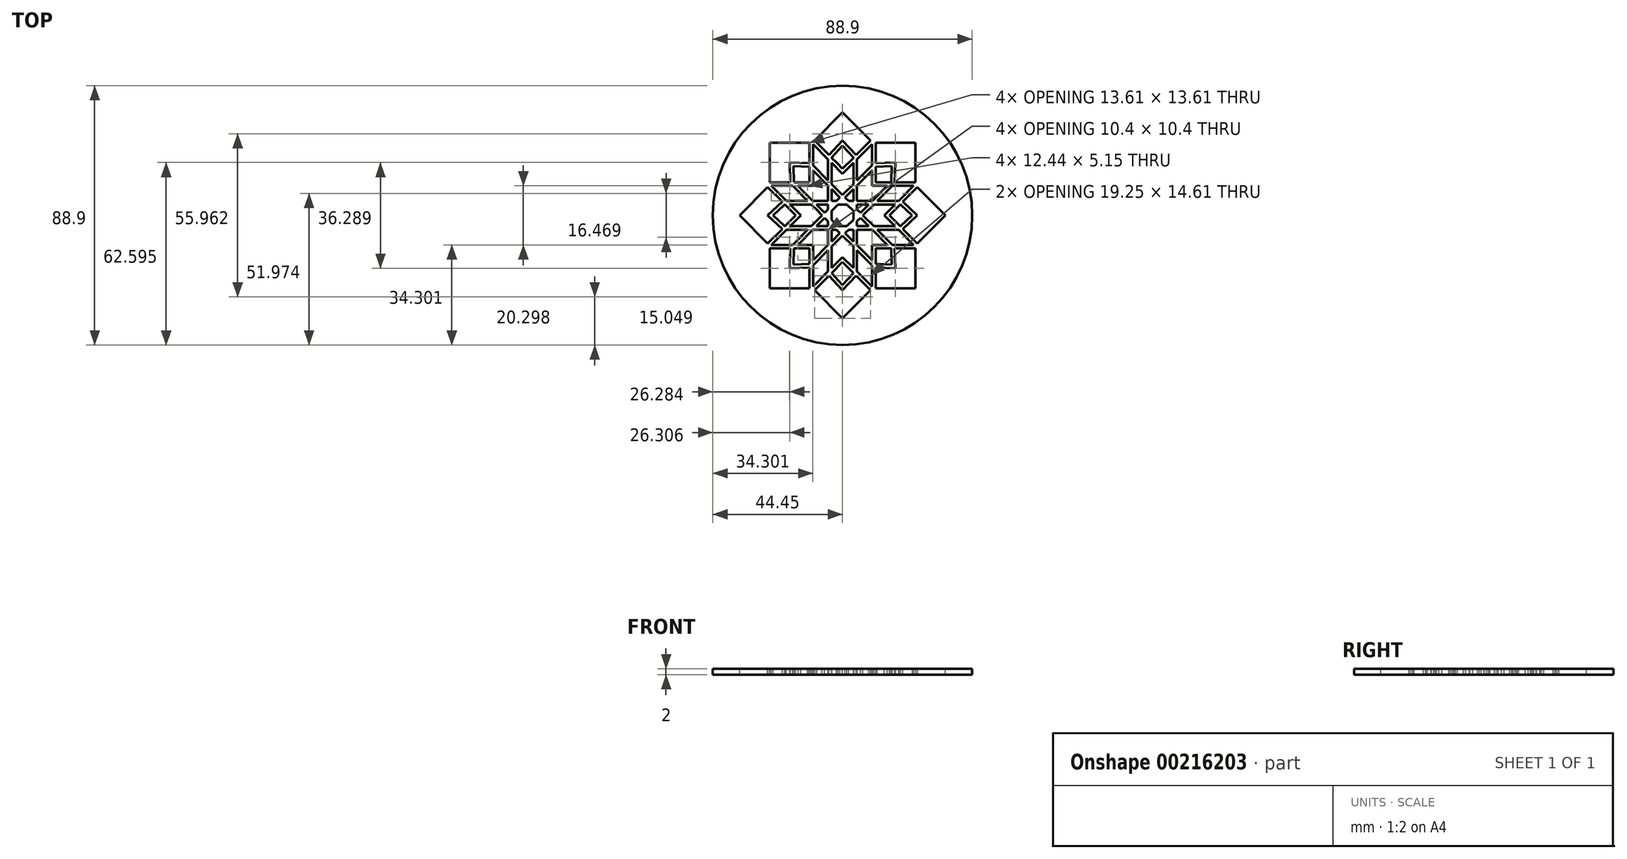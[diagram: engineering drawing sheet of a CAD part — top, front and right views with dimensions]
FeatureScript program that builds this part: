
annotation { "Feature Type Name" : "Feature", "Feature Type Description" : "" }
export const myFeature = defineFeature(function(context is Context, id is Id, definition is map)
    precondition{}
    {
        {
            var Q0;
            Q0=qCreatedBy(makeId("Top.planeOp"),FACE);
            var sketch = newSketch(context, id + "F0", { "sketchPlane" : qUnion([Q0])});
            skLineSegment(sketch, "E0.bottom", {"start": v(-44.45, 44.45) * mm, "end": v(44.45, 44.45) * mm});
            skLineSegment(sketch, "E0.top", {"start": v(-44.45, -44.45) * mm, "end": v(44.45, -44.45) * mm});
            skLineSegment(sketch, "E0.left", {"start": v(-44.45, 44.45) * mm, "end": v(-44.45, -44.45) * mm});
            skLineSegment(sketch, "E0.right", {"start": v(44.45, 44.45) * mm, "end": v(44.45, -44.45) * mm});
            skSolve(sketch);
        }
        {
            var Q0;
            Q0 = qSketchRegion(id + "F0", true);
            extrude(context, id + "F1", {"entities" : qUnion([Q0]), "oppositeDirection" : true, "depth" : 2 * mm});
        }
        {
            var Q0;
            Q0=qCreatedBy(makeId("Top.planeOp"),FACE);
            var sketch = newSketch(context, id + "F2", { "sketchPlane" : qUnion([Q0])});
            skLineSegment(sketch, "E1", {"start": v(0.87, 6.12) * mm, "end": v(2.05, 4.95) * mm});
            skLineSegment(sketch, "E2", {"start": v(2.05, 4.95) * mm, "end": v(3.71, 4.95) * mm});
            skLineSegment(sketch, "E3", {"start": v(3.71, 4.95) * mm, "end": v(3.71, 8.96) * mm});
            skLineSegment(sketch, "E4", {"start": v(3.71, 8.96) * mm, "end": v(0.87, 6.12) * mm});
            skLineSegment(sketch, "E5", {"start": v(-3.71, 4.95) * mm, "end": v(-2.05, 4.95) * mm});
            skLineSegment(sketch, "E6", {"start": v(-2.05, 4.95) * mm, "end": v(-0.88, 6.12) * mm});
            skLineSegment(sketch, "E7", {"start": v(-0.88, 6.12) * mm, "end": v(-3.71, 8.96) * mm});
            skLineSegment(sketch, "E8", {"start": v(-3.71, 8.96) * mm, "end": v(-3.71, 4.95) * mm});
            skLineSegment(sketch, "E9", {"start": v(4.95, 3.71) * mm, "end": v(4.95, 2.05) * mm});
            skLineSegment(sketch, "E10", {"start": v(4.95, 2.05) * mm, "end": v(6.12, 0.88) * mm});
            skLineSegment(sketch, "E11", {"start": v(6.12, 0.88) * mm, "end": v(8.96, 3.71) * mm});
            skLineSegment(sketch, "E12", {"start": v(8.96, 3.71) * mm, "end": v(4.95, 3.71) * mm});
            skLineSegment(sketch, "E13", {"start": v(-0.88, -6.12) * mm, "end": v(-2.05, -4.95) * mm});
            skLineSegment(sketch, "E14", {"start": v(-2.05, -4.95) * mm, "end": v(-3.71, -4.95) * mm});
            skLineSegment(sketch, "E15", {"start": v(-3.71, -4.95) * mm, "end": v(-3.71, -8.96) * mm});
            skLineSegment(sketch, "E16", {"start": v(-3.71, -8.96) * mm, "end": v(-0.88, -6.12) * mm});
            skLineSegment(sketch, "E17", {"start": v(-4.95, -2.05) * mm, "end": v(-6.12, -0.87) * mm});
            skLineSegment(sketch, "E18", {"start": v(-6.12, -0.87) * mm, "end": v(-8.96, -3.71) * mm});
            skLineSegment(sketch, "E19", {"start": v(-8.96, -3.71) * mm, "end": v(-4.95, -3.71) * mm});
            skLineSegment(sketch, "E20", {"start": v(-4.95, -3.71) * mm, "end": v(-4.95, -2.05) * mm});
            skLineSegment(sketch, "E21", {"start": v(-14.28, 0) * mm, "end": v(-18, -3.71) * mm});
            skLineSegment(sketch, "E22", {"start": v(-18, -3.71) * mm, "end": v(-10.71, -3.71) * mm});
            skLineSegment(sketch, "E23", {"start": v(-10.71, -3.71) * mm, "end": v(-7, 0) * mm});
            skLineSegment(sketch, "E24", {"start": v(-7, 0) * mm, "end": v(-10.71, 3.71) * mm});
            skLineSegment(sketch, "E25", {"start": v(-10.71, 3.71) * mm, "end": v(-18, 3.71) * mm});
            skLineSegment(sketch, "E26", {"start": v(-18, 3.71) * mm, "end": v(-14.28, 0) * mm});
            skLineSegment(sketch, "E27", {"start": v(-8.96, 3.71) * mm, "end": v(-6.12, 0.88) * mm});
            skLineSegment(sketch, "E28", {"start": v(0, -7) * mm, "end": v(-3.71, -10.7) * mm});
            skLineSegment(sketch, "E29", {"start": v(-3.71, -10.7) * mm, "end": v(-3.71, -18) * mm});
            skLineSegment(sketch, "E30", {"start": v(-3.71, -18) * mm, "end": v(0, -14.28) * mm});
            skLineSegment(sketch, "E31", {"start": v(0, -14.28) * mm, "end": v(3.71, -18) * mm});
            skLineSegment(sketch, "E32", {"start": v(3.71, -18) * mm, "end": v(3.71, -10.7) * mm});
            skLineSegment(sketch, "E33", {"start": v(3.71, -10.7) * mm, "end": v(0, -7) * mm});
            skLineSegment(sketch, "E34", {"start": v(-10.1, -17.1) * mm, "end": v(-10.1, -24.38) * mm});
            skLineSegment(sketch, "E35", {"start": v(-10.1, -24.38) * mm, "end": v(-4.95, -19.23) * mm});
            skLineSegment(sketch, "E36", {"start": v(-4.95, -19.23) * mm, "end": v(-4.95, -11.95) * mm});
            skLineSegment(sketch, "E37", {"start": v(-4.95, -11.95) * mm, "end": v(-10.1, -17.1) * mm});
            skLineSegment(sketch, "E38", {"start": v(1.54, -3.71) * mm, "end": v(3.71, -1.54) * mm});
            skLineSegment(sketch, "E39", {"start": v(3.71, -1.54) * mm, "end": v(3.71, 1.54) * mm});
            skLineSegment(sketch, "E40", {"start": v(3.71, 1.54) * mm, "end": v(1.54, 3.71) * mm});
            skLineSegment(sketch, "E41", {"start": v(1.54, 3.71) * mm, "end": v(-1.54, 3.71) * mm});
            skLineSegment(sketch, "E42", {"start": v(-1.54, 3.71) * mm, "end": v(-3.71, 1.54) * mm});
            skLineSegment(sketch, "E43", {"start": v(-3.71, 1.54) * mm, "end": v(-3.71, -1.54) * mm});
            skLineSegment(sketch, "E44", {"start": v(-3.71, -1.54) * mm, "end": v(-1.54, -3.71) * mm});
            skLineSegment(sketch, "E45", {"start": v(-1.54, -3.71) * mm, "end": v(1.54, -3.71) * mm});
            skLineSegment(sketch, "E46", {"start": v(3.71, -19.86) * mm, "end": v(3.71, -19.75) * mm});
            skLineSegment(sketch, "E47", {"start": v(3.71, -19.75) * mm, "end": v(0, -16.03) * mm});
            skLineSegment(sketch, "E48", {"start": v(0, -16.03) * mm, "end": v(-3.71, -19.74) * mm});
            skLineSegment(sketch, "E49", {"start": v(-3.71, -19.74) * mm, "end": v(-3.71, -19.86) * mm});
            skLineSegment(sketch, "E50", {"start": v(-3.71, -19.86) * mm, "end": v(0, -23.84) * mm});
            skLineSegment(sketch, "E51", {"start": v(0, -23.84) * mm, "end": v(3.71, -19.86) * mm});
            skLineSegment(sketch, "E52", {"start": v(11.34, -16.59) * mm, "end": v(11.42, -16.67) * mm});
            skLineSegment(sketch, "E53", {"start": v(11.42, -16.67) * mm, "end": v(16.86, -16.86) * mm});
            skLineSegment(sketch, "E54", {"start": v(16.86, -16.86) * mm, "end": v(16.67, -11.42) * mm});
            skLineSegment(sketch, "E55", {"start": v(16.67, -11.42) * mm, "end": v(16.59, -11.34) * mm});
            skLineSegment(sketch, "E56", {"start": v(16.59, -11.34) * mm, "end": v(11.34, -11.34) * mm});
            skLineSegment(sketch, "E57", {"start": v(11.34, -11.34) * mm, "end": v(11.34, -16.59) * mm});
            skLineSegment(sketch, "E58", {"start": v(-19.75, 3.71) * mm, "end": v(-19.86, 3.71) * mm});
            skLineSegment(sketch, "E59", {"start": v(-19.86, 3.71) * mm, "end": v(-23.84, 0) * mm});
            skLineSegment(sketch, "E60", {"start": v(-23.84, 0) * mm, "end": v(-19.86, -3.71) * mm});
            skLineSegment(sketch, "E61", {"start": v(-19.86, -3.71) * mm, "end": v(-19.75, -3.71) * mm});
            skLineSegment(sketch, "E62", {"start": v(-19.75, -3.71) * mm, "end": v(-16.03, 0) * mm});
            skLineSegment(sketch, "E63", {"start": v(-16.03, 0) * mm, "end": v(-19.75, 3.71) * mm});
            skLineSegment(sketch, "E64", {"start": v(10.1, 17.1) * mm, "end": v(10.1, 24.39) * mm});
            skLineSegment(sketch, "E65", {"start": v(10.1, 24.39) * mm, "end": v(4.95, 19.23) * mm});
            skLineSegment(sketch, "E66", {"start": v(4.95, 19.23) * mm, "end": v(4.95, 11.95) * mm});
            skLineSegment(sketch, "E67", {"start": v(4.95, 11.95) * mm, "end": v(10.1, 17.1) * mm});
            skLineSegment(sketch, "E68", {"start": v(19.75, -3.71) * mm, "end": v(19.86, -3.71) * mm});
            skLineSegment(sketch, "E69", {"start": v(19.86, -3.71) * mm, "end": v(23.84, 0) * mm});
            skLineSegment(sketch, "E70", {"start": v(23.84, 0) * mm, "end": v(19.86, 3.71) * mm});
            skLineSegment(sketch, "E71", {"start": v(19.86, 3.71) * mm, "end": v(19.75, 3.71) * mm});
            skLineSegment(sketch, "E72", {"start": v(19.75, 3.71) * mm, "end": v(16.03, 0) * mm});
            skLineSegment(sketch, "E73", {"start": v(16.03, 0) * mm, "end": v(19.75, -3.71) * mm});
            skLineSegment(sketch, "E74", {"start": v(0, 7) * mm, "end": v(3.71, 10.71) * mm});
            skLineSegment(sketch, "E75", {"start": v(3.71, 10.71) * mm, "end": v(3.71, 18) * mm});
            skLineSegment(sketch, "E76", {"start": v(3.71, 18) * mm, "end": v(0, 14.29) * mm});
            skLineSegment(sketch, "E77", {"start": v(0, 14.29) * mm, "end": v(-3.71, 18) * mm});
            skLineSegment(sketch, "E78", {"start": v(-3.71, 18) * mm, "end": v(-3.71, 10.71) * mm});
            skLineSegment(sketch, "E79", {"start": v(-3.71, 10.71) * mm, "end": v(0, 7) * mm});
            skLineSegment(sketch, "E80", {"start": v(-3.71, 19.86) * mm, "end": v(-3.71, 19.75) * mm});
            skLineSegment(sketch, "E81", {"start": v(-3.71, 19.75) * mm, "end": v(0, 16.03) * mm});
            skLineSegment(sketch, "E82", {"start": v(0, 16.03) * mm, "end": v(3.71, 19.75) * mm});
            skLineSegment(sketch, "E83", {"start": v(3.71, 19.75) * mm, "end": v(3.71, 19.86) * mm});
            skLineSegment(sketch, "E84", {"start": v(3.71, 19.86) * mm, "end": v(0, 23.84) * mm});
            skLineSegment(sketch, "E85", {"start": v(0, 23.84) * mm, "end": v(-3.71, 19.86) * mm});
            skLineSegment(sketch, "E86", {"start": v(10.1, -17.1) * mm, "end": v(4.95, -11.95) * mm});
            skLineSegment(sketch, "E87", {"start": v(4.95, -11.95) * mm, "end": v(4.95, -19.23) * mm});
            skLineSegment(sketch, "E88", {"start": v(4.95, -19.23) * mm, "end": v(10.1, -24.38) * mm});
            skLineSegment(sketch, "E89", {"start": v(10.1, -24.38) * mm, "end": v(10.1, -17.1) * mm});
            skLineSegment(sketch, "E90", {"start": v(11.34, 17.9) * mm, "end": v(18.14, 18.14) * mm});
            skLineSegment(sketch, "E91", {"start": v(18.14, 18.14) * mm, "end": v(17.9, 11.34) * mm});
            skLineSegment(sketch, "E92", {"start": v(17.9, 11.34) * mm, "end": v(24.95, 11.34) * mm});
            skLineSegment(sketch, "E93", {"start": v(24.95, 11.34) * mm, "end": v(24.95, 24.95) * mm});
            skLineSegment(sketch, "E94", {"start": v(24.95, 24.95) * mm, "end": v(11.34, 24.95) * mm});
            skLineSegment(sketch, "E95", {"start": v(11.34, 24.95) * mm, "end": v(11.34, 17.9) * mm});
            skLineSegment(sketch, "E96", {"start": v(0, 25.65) * mm, "end": v(4.64, 20.68) * mm});
            skLineSegment(sketch, "E97", {"start": v(4.64, 20.68) * mm, "end": v(9.63, 25.66) * mm});
            skLineSegment(sketch, "E98", {"start": v(9.63, 25.66) * mm, "end": v(0, 35.29) * mm});
            skLineSegment(sketch, "E99", {"start": v(0, 35.29) * mm, "end": v(-9.63, 25.66) * mm});
            skLineSegment(sketch, "E100", {"start": v(-9.63, 25.66) * mm, "end": v(-4.64, 20.68) * mm});
            skLineSegment(sketch, "E101", {"start": v(-4.64, 20.68) * mm, "end": v(0, 25.65) * mm});
            skLineSegment(sketch, "E102", {"start": v(20.68, 4.64) * mm, "end": v(25.65, 0) * mm});
            skLineSegment(sketch, "E103", {"start": v(25.65, 0) * mm, "end": v(20.68, -4.64) * mm});
            skLineSegment(sketch, "E104", {"start": v(20.68, -4.64) * mm, "end": v(25.66, -9.63) * mm});
            skLineSegment(sketch, "E105", {"start": v(25.66, -9.63) * mm, "end": v(35.29, 0) * mm});
            skLineSegment(sketch, "E106", {"start": v(35.29, 0) * mm, "end": v(25.66, 9.63) * mm});
            skLineSegment(sketch, "E107", {"start": v(25.66, 9.63) * mm, "end": v(20.68, 4.64) * mm});
            skLineSegment(sketch, "E108", {"start": v(-18.14, 18.14) * mm, "end": v(-11.34, 17.9) * mm});
            skLineSegment(sketch, "E109", {"start": v(-11.34, 17.9) * mm, "end": v(-11.34, 24.95) * mm});
            skLineSegment(sketch, "E110", {"start": v(-11.34, 24.95) * mm, "end": v(-24.95, 24.95) * mm});
            skLineSegment(sketch, "E111", {"start": v(-24.95, 24.95) * mm, "end": v(-24.95, 11.34) * mm});
            skLineSegment(sketch, "E112", {"start": v(-24.95, 11.34) * mm, "end": v(-17.9, 11.34) * mm});
            skLineSegment(sketch, "E113", {"start": v(-17.9, 11.34) * mm, "end": v(-18.14, 18.14) * mm});
            skLineSegment(sketch, "E114", {"start": v(15.35, -10.1) * mm, "end": v(10.2, -4.95) * mm});
            skLineSegment(sketch, "E115", {"start": v(10.2, -4.95) * mm, "end": v(4.95, -4.95) * mm});
            skLineSegment(sketch, "E116", {"start": v(4.95, -4.95) * mm, "end": v(4.95, -10.2) * mm});
            skLineSegment(sketch, "E117", {"start": v(4.95, -10.2) * mm, "end": v(10.1, -15.35) * mm});
            skLineSegment(sketch, "E118", {"start": v(10.1, -15.35) * mm, "end": v(10.1, -10.1) * mm});
            skLineSegment(sketch, "E119", {"start": v(10.1, -10.1) * mm, "end": v(15.35, -10.1) * mm});
            skLineSegment(sketch, "E120", {"start": v(19.23, -4.95) * mm, "end": v(11.95, -4.95) * mm});
            skLineSegment(sketch, "E121", {"start": v(11.95, -4.95) * mm, "end": v(17.1, -10.1) * mm});
            skLineSegment(sketch, "E122", {"start": v(17.1, -10.1) * mm, "end": v(24.38, -10.1) * mm});
            skLineSegment(sketch, "E123", {"start": v(24.38, -10.1) * mm, "end": v(19.23, -4.95) * mm});
            skLineSegment(sketch, "E124", {"start": v(-20.68, -4.64) * mm, "end": v(-25.65, 0) * mm});
            skLineSegment(sketch, "E125", {"start": v(-25.65, 0) * mm, "end": v(-20.68, 4.64) * mm});
            skLineSegment(sketch, "E126", {"start": v(-20.68, 4.64) * mm, "end": v(-25.66, 9.63) * mm});
            skLineSegment(sketch, "E127", {"start": v(-25.66, 9.63) * mm, "end": v(-35.29, 0) * mm});
            skLineSegment(sketch, "E128", {"start": v(-35.29, 0) * mm, "end": v(-25.66, -9.63) * mm});
            skLineSegment(sketch, "E129", {"start": v(-25.66, -9.63) * mm, "end": v(-20.68, -4.64) * mm});
            skLineSegment(sketch, "E130", {"start": v(-4.95, -10.2) * mm, "end": v(-4.95, -4.95) * mm});
            skLineSegment(sketch, "E131", {"start": v(-4.95, -4.95) * mm, "end": v(-10.2, -4.95) * mm});
            skLineSegment(sketch, "E132", {"start": v(-10.2, -4.95) * mm, "end": v(-15.35, -10.1) * mm});
            skLineSegment(sketch, "E133", {"start": v(-15.35, -10.1) * mm, "end": v(-10.1, -10.1) * mm});
            skLineSegment(sketch, "E134", {"start": v(-10.1, -10.1) * mm, "end": v(-10.1, -15.35) * mm});
            skLineSegment(sketch, "E135", {"start": v(-10.1, -15.35) * mm, "end": v(-4.95, -10.2) * mm});
            skLineSegment(sketch, "E136", {"start": v(3.71, -4.95) * mm, "end": v(2.05, -4.95) * mm});
            skLineSegment(sketch, "E137", {"start": v(2.05, -4.95) * mm, "end": v(0.87, -6.12) * mm});
            skLineSegment(sketch, "E138", {"start": v(0.87, -6.12) * mm, "end": v(3.71, -8.96) * mm});
            skLineSegment(sketch, "E139", {"start": v(3.71, -8.96) * mm, "end": v(3.71, -4.95) * mm});
            skLineSegment(sketch, "E140", {"start": v(0, -35.29) * mm, "end": v(9.63, -25.66) * mm});
            skLineSegment(sketch, "E141", {"start": v(9.63, -25.66) * mm, "end": v(4.64, -20.68) * mm});
            skLineSegment(sketch, "E142", {"start": v(4.64, -20.68) * mm, "end": v(0, -25.65) * mm});
            skLineSegment(sketch, "E143", {"start": v(0, -25.65) * mm, "end": v(-4.64, -20.68) * mm});
            skLineSegment(sketch, "E144", {"start": v(-4.64, -20.68) * mm, "end": v(-9.63, -25.66) * mm});
            skLineSegment(sketch, "E145", {"start": v(-9.63, -25.66) * mm, "end": v(0, -35.29) * mm});
            skLineSegment(sketch, "E146", {"start": v(18.14, -18.14) * mm, "end": v(11.34, -17.9) * mm});
            skLineSegment(sketch, "E147", {"start": v(11.34, -17.9) * mm, "end": v(11.34, -24.95) * mm});
            skLineSegment(sketch, "E148", {"start": v(11.34, -24.95) * mm, "end": v(24.95, -24.95) * mm});
            skLineSegment(sketch, "E149", {"start": v(24.95, -24.95) * mm, "end": v(24.95, -11.34) * mm});
            skLineSegment(sketch, "E150", {"start": v(24.95, -11.34) * mm, "end": v(17.9, -11.34) * mm});
            skLineSegment(sketch, "E151", {"start": v(17.9, -11.34) * mm, "end": v(18.14, -18.14) * mm});
            skLineSegment(sketch, "E152", {"start": v(14.28, 0) * mm, "end": v(18, 3.71) * mm});
            skLineSegment(sketch, "E153", {"start": v(18, 3.71) * mm, "end": v(10.7, 3.71) * mm});
            skLineSegment(sketch, "E154", {"start": v(10.7, 3.71) * mm, "end": v(7, 0) * mm});
            skLineSegment(sketch, "E155", {"start": v(7, 0) * mm, "end": v(10.7, -3.71) * mm});
            skLineSegment(sketch, "E156", {"start": v(10.7, -3.71) * mm, "end": v(18, -3.71) * mm});
            skLineSegment(sketch, "E157", {"start": v(18, -3.71) * mm, "end": v(14.28, 0) * mm});
            skLineSegment(sketch, "E158", {"start": v(4.95, 10.2) * mm, "end": v(4.95, 4.95) * mm});
            skLineSegment(sketch, "E159", {"start": v(4.95, 4.95) * mm, "end": v(10.2, 4.95) * mm});
            skLineSegment(sketch, "E160", {"start": v(10.2, 4.95) * mm, "end": v(15.35, 10.1) * mm});
            skLineSegment(sketch, "E161", {"start": v(15.35, 10.1) * mm, "end": v(10.1, 10.1) * mm});
            skLineSegment(sketch, "E162", {"start": v(10.1, 10.1) * mm, "end": v(10.1, 15.35) * mm});
            skLineSegment(sketch, "E163", {"start": v(10.1, 15.35) * mm, "end": v(4.95, 10.2) * mm});
            skLineSegment(sketch, "E164", {"start": v(11.34, 16.59) * mm, "end": v(11.34, 11.34) * mm});
            skLineSegment(sketch, "E165", {"start": v(11.34, 11.34) * mm, "end": v(16.59, 11.34) * mm});
            skLineSegment(sketch, "E166", {"start": v(16.59, 11.34) * mm, "end": v(16.67, 11.42) * mm});
            skLineSegment(sketch, "E167", {"start": v(16.67, 11.42) * mm, "end": v(16.86, 16.86) * mm});
            skLineSegment(sketch, "E168", {"start": v(16.86, 16.86) * mm, "end": v(11.42, 16.67) * mm});
            skLineSegment(sketch, "E169", {"start": v(11.42, 16.67) * mm, "end": v(11.34, 16.59) * mm});
            skLineSegment(sketch, "E170", {"start": v(17.1, 10.1) * mm, "end": v(11.95, 4.95) * mm});
            skLineSegment(sketch, "E171", {"start": v(11.95, 4.95) * mm, "end": v(19.23, 4.95) * mm});
            skLineSegment(sketch, "E172", {"start": v(19.23, 4.95) * mm, "end": v(24.38, 10.1) * mm});
            skLineSegment(sketch, "E173", {"start": v(24.38, 10.1) * mm, "end": v(17.1, 10.1) * mm});
            skLineSegment(sketch, "E174", {"start": v(6.12, -0.87) * mm, "end": v(4.95, -2.05) * mm});
            skLineSegment(sketch, "E175", {"start": v(4.95, -2.05) * mm, "end": v(4.95, -3.71) * mm});
            skLineSegment(sketch, "E176", {"start": v(4.95, -3.71) * mm, "end": v(8.96, -3.71) * mm});
            skLineSegment(sketch, "E177", {"start": v(8.96, -3.71) * mm, "end": v(6.12, -0.87) * mm});
            skLineSegment(sketch, "E178", {"start": v(-24.38, -10.1) * mm, "end": v(-17.1, -10.1) * mm});
            skLineSegment(sketch, "E179", {"start": v(-10.1, 17.1) * mm, "end": v(-4.95, 11.95) * mm});
            skLineSegment(sketch, "E180", {"start": v(-4.95, 11.95) * mm, "end": v(-4.95, 19.23) * mm});
            skLineSegment(sketch, "E181", {"start": v(-4.95, 19.23) * mm, "end": v(-10.1, 24.39) * mm});
            skLineSegment(sketch, "E182", {"start": v(-10.1, 24.39) * mm, "end": v(-10.1, 17.1) * mm});
            skLineSegment(sketch, "E183", {"start": v(-19.23, 4.95) * mm, "end": v(-11.95, 4.95) * mm});
            skLineSegment(sketch, "E184", {"start": v(-11.95, 4.95) * mm, "end": v(-17.1, 10.1) * mm});
            skLineSegment(sketch, "E185", {"start": v(-17.1, 10.1) * mm, "end": v(-24.39, 10.1) * mm});
            skLineSegment(sketch, "E186", {"start": v(-24.39, 10.1) * mm, "end": v(-19.23, 4.95) * mm});
            skLineSegment(sketch, "E187", {"start": v(-15.35, 10.1) * mm, "end": v(-10.2, 4.95) * mm});
            skLineSegment(sketch, "E188", {"start": v(-10.2, 4.95) * mm, "end": v(-4.95, 4.95) * mm});
            skLineSegment(sketch, "E189", {"start": v(-4.95, 4.95) * mm, "end": v(-4.95, 10.2) * mm});
            skLineSegment(sketch, "E190", {"start": v(-4.95, 10.2) * mm, "end": v(-10.1, 15.35) * mm});
            skLineSegment(sketch, "E191", {"start": v(-10.1, 15.35) * mm, "end": v(-10.1, 10.1) * mm});
            skLineSegment(sketch, "E192", {"start": v(-10.1, 10.1) * mm, "end": v(-15.35, 10.1) * mm});
            skLineSegment(sketch, "E193", {"start": v(-11.34, -16.59) * mm, "end": v(-11.34, -11.34) * mm});
            skLineSegment(sketch, "E194", {"start": v(-11.34, -11.34) * mm, "end": v(-16.59, -11.34) * mm});
            skLineSegment(sketch, "E195", {"start": v(-16.59, -11.34) * mm, "end": v(-16.67, -11.42) * mm});
            skLineSegment(sketch, "E196", {"start": v(-16.67, -11.42) * mm, "end": v(-16.86, -16.86) * mm});
            skLineSegment(sketch, "E197", {"start": v(-16.86, -16.86) * mm, "end": v(-11.42, -16.67) * mm});
            skLineSegment(sketch, "E198", {"start": v(-11.42, -16.67) * mm, "end": v(-11.34, -16.59) * mm});
            skLineSegment(sketch, "E199", {"start": v(16.67, -11.42) * mm, "end": v(16.86, -16.86) * mm});
            skLineSegment(sketch, "E200", {"start": v(16.86, -16.86) * mm, "end": v(11.42, -16.67) * mm});
            skLineSegment(sketch, "E201", {"start": v(11.42, -16.67) * mm, "end": v(11.34, -16.59) * mm});
            skLineSegment(sketch, "E202", {"start": v(11.34, -16.59) * mm, "end": v(11.34, -11.34) * mm});
            skLineSegment(sketch, "E203", {"start": v(11.34, -11.34) * mm, "end": v(16.59, -11.34) * mm});
            skLineSegment(sketch, "E204", {"start": v(16.59, -11.34) * mm, "end": v(16.67, -11.42) * mm});
            skLineSegment(sketch, "E205", {"start": v(-3.71, -19.74) * mm, "end": v(0, -16.03) * mm});
            skLineSegment(sketch, "E206", {"start": v(0, -16.03) * mm, "end": v(3.71, -19.75) * mm});
            skLineSegment(sketch, "E207", {"start": v(3.71, -19.75) * mm, "end": v(3.71, -19.86) * mm});
            skLineSegment(sketch, "E208", {"start": v(3.71, -19.86) * mm, "end": v(0, -23.84) * mm});
            skLineSegment(sketch, "E209", {"start": v(0, -23.84) * mm, "end": v(-3.71, -19.86) * mm});
            skLineSegment(sketch, "E210", {"start": v(-3.71, -19.86) * mm, "end": v(-3.71, -19.74) * mm});
            skLineSegment(sketch, "E211", {"start": v(0, -14.28) * mm, "end": v(-3.71, -18) * mm});
            skLineSegment(sketch, "E212", {"start": v(-3.71, -18) * mm, "end": v(-3.71, -10.7) * mm});
            skLineSegment(sketch, "E213", {"start": v(-3.71, -10.7) * mm, "end": v(0, -7) * mm});
            skLineSegment(sketch, "E214", {"start": v(0, -7) * mm, "end": v(3.71, -10.7) * mm});
            skLineSegment(sketch, "E215", {"start": v(3.71, -10.7) * mm, "end": v(3.71, -18) * mm});
            skLineSegment(sketch, "E216", {"start": v(3.71, -18) * mm, "end": v(0, -14.28) * mm});
            skLineSegment(sketch, "E217", {"start": v(-10.1, -24.38) * mm, "end": v(-10.1, -17.1) * mm});
            skLineSegment(sketch, "E218", {"start": v(-10.1, -17.1) * mm, "end": v(-4.95, -11.95) * mm});
            skLineSegment(sketch, "E219", {"start": v(-4.95, -11.95) * mm, "end": v(-4.95, -19.23) * mm});
            skLineSegment(sketch, "E220", {"start": v(-4.95, -19.23) * mm, "end": v(-10.1, -24.38) * mm});
            skLineSegment(sketch, "E221", {"start": v(-19.86, -3.71) * mm, "end": v(-23.84, 0) * mm});
            skLineSegment(sketch, "E222", {"start": v(-23.84, 0) * mm, "end": v(-19.86, 3.71) * mm});
            skLineSegment(sketch, "E223", {"start": v(-19.86, 3.71) * mm, "end": v(-19.75, 3.71) * mm});
            skLineSegment(sketch, "E224", {"start": v(-19.75, 3.71) * mm, "end": v(-16.03, 0) * mm});
            skLineSegment(sketch, "E225", {"start": v(-16.03, 0) * mm, "end": v(-19.75, -3.71) * mm});
            skLineSegment(sketch, "E226", {"start": v(-19.75, -3.71) * mm, "end": v(-19.86, -3.71) * mm});
            skLineSegment(sketch, "E227", {"start": v(3.71, 19.75) * mm, "end": v(0, 16.03) * mm});
            skLineSegment(sketch, "E228", {"start": v(0, 16.03) * mm, "end": v(-3.71, 19.75) * mm});
            skLineSegment(sketch, "E229", {"start": v(-3.71, 19.75) * mm, "end": v(-3.71, 19.86) * mm});
            skLineSegment(sketch, "E230", {"start": v(-3.71, 19.86) * mm, "end": v(0, 23.84) * mm});
            skLineSegment(sketch, "E231", {"start": v(0, 23.84) * mm, "end": v(3.71, 19.86) * mm});
            skLineSegment(sketch, "E232", {"start": v(3.71, 19.86) * mm, "end": v(3.71, 19.75) * mm});
            skLineSegment(sketch, "E233", {"start": v(0, 14.28) * mm, "end": v(3.71, 18) * mm});
            skLineSegment(sketch, "E234", {"start": v(3.71, 18) * mm, "end": v(3.71, 10.71) * mm});
            skLineSegment(sketch, "E235", {"start": v(3.71, 10.71) * mm, "end": v(0, 7) * mm});
            skLineSegment(sketch, "E236", {"start": v(0, 7) * mm, "end": v(-3.71, 10.71) * mm});
            skLineSegment(sketch, "E237", {"start": v(-3.71, 10.71) * mm, "end": v(-3.71, 18) * mm});
            skLineSegment(sketch, "E238", {"start": v(-3.71, 18) * mm, "end": v(0, 14.28) * mm});
            skLineSegment(sketch, "E239", {"start": v(10.1, 24.39) * mm, "end": v(10.1, 17.1) * mm});
            skLineSegment(sketch, "E240", {"start": v(10.1, 17.1) * mm, "end": v(4.95, 11.95) * mm});
            skLineSegment(sketch, "E241", {"start": v(4.95, 11.95) * mm, "end": v(4.95, 19.23) * mm});
            skLineSegment(sketch, "E242", {"start": v(4.95, 19.23) * mm, "end": v(10.1, 24.39) * mm});
            skLineSegment(sketch, "E243", {"start": v(19.86, 3.71) * mm, "end": v(23.84, 0) * mm});
            skLineSegment(sketch, "E244", {"start": v(23.84, 0) * mm, "end": v(19.86, -3.71) * mm});
            skLineSegment(sketch, "E245", {"start": v(19.86, -3.71) * mm, "end": v(19.75, -3.71) * mm});
            skLineSegment(sketch, "E246", {"start": v(19.75, -3.71) * mm, "end": v(16.03, 0) * mm});
            skLineSegment(sketch, "E247", {"start": v(16.03, 0) * mm, "end": v(19.75, 3.71) * mm});
            skLineSegment(sketch, "E248", {"start": v(19.75, 3.71) * mm, "end": v(19.86, 3.71) * mm});
            skLineSegment(sketch, "E249", {"start": v(-3.71, 1.54) * mm, "end": v(-1.54, 3.71) * mm});
            skLineSegment(sketch, "E250", {"start": v(-1.54, 3.71) * mm, "end": v(1.54, 3.71) * mm});
            skLineSegment(sketch, "E251", {"start": v(1.54, 3.71) * mm, "end": v(3.71, 1.54) * mm});
            skLineSegment(sketch, "E252", {"start": v(3.71, 1.54) * mm, "end": v(3.71, -1.54) * mm});
            skLineSegment(sketch, "E253", {"start": v(3.71, -1.54) * mm, "end": v(1.54, -3.71) * mm});
            skLineSegment(sketch, "E254", {"start": v(1.54, -3.71) * mm, "end": v(-1.54, -3.71) * mm});
            skLineSegment(sketch, "E255", {"start": v(-1.54, -3.71) * mm, "end": v(-3.71, -1.54) * mm});
            skLineSegment(sketch, "E256", {"start": v(-3.71, -1.54) * mm, "end": v(-3.71, 1.54) * mm});
            skLineSegment(sketch, "E257", {"start": v(4.95, 2.05) * mm, "end": v(4.95, 3.71) * mm});
            skLineSegment(sketch, "E258", {"start": v(4.95, 3.71) * mm, "end": v(8.96, 3.71) * mm});
            skLineSegment(sketch, "E259", {"start": v(8.96, 3.71) * mm, "end": v(6.12, 0.88) * mm});
            skLineSegment(sketch, "E260", {"start": v(6.12, 0.88) * mm, "end": v(4.95, 2.05) * mm});
            skLineSegment(sketch, "E261", {"start": v(2.05, 4.95) * mm, "end": v(0.87, 6.12) * mm});
            skLineSegment(sketch, "E262", {"start": v(0.87, 6.12) * mm, "end": v(3.71, 8.96) * mm});
            skLineSegment(sketch, "E263", {"start": v(3.71, 8.96) * mm, "end": v(3.71, 4.95) * mm});
            skLineSegment(sketch, "E264", {"start": v(3.71, 4.95) * mm, "end": v(2.05, 4.95) * mm});
            skLineSegment(sketch, "E265", {"start": v(-2.05, 4.95) * mm, "end": v(-3.71, 4.95) * mm});
            skLineSegment(sketch, "E266", {"start": v(-3.71, 4.95) * mm, "end": v(-3.71, 8.96) * mm});
            skLineSegment(sketch, "E267", {"start": v(-3.71, 8.96) * mm, "end": v(-0.88, 6.12) * mm});
            skLineSegment(sketch, "E268", {"start": v(-0.88, 6.12) * mm, "end": v(-2.05, 4.95) * mm});
            skLineSegment(sketch, "E269", {"start": v(-4.95, 2.05) * mm, "end": v(-6.12, 0.88) * mm});
            skLineSegment(sketch, "E270", {"start": v(-8.96, 3.71) * mm, "end": v(-4.95, 3.71) * mm});
            skLineSegment(sketch, "E271", {"start": v(-4.95, 3.71) * mm, "end": v(-4.95, 2.05) * mm});
            skLineSegment(sketch, "E272", {"start": v(-7, 0) * mm, "end": v(-10.71, -3.71) * mm});
            skLineSegment(sketch, "E273", {"start": v(-10.71, -3.71) * mm, "end": v(-18, -3.71) * mm});
            skLineSegment(sketch, "E274", {"start": v(-18, -3.71) * mm, "end": v(-14.29, 0) * mm});
            skLineSegment(sketch, "E275", {"start": v(-14.29, 0) * mm, "end": v(-18, 3.71) * mm});
            skLineSegment(sketch, "E276", {"start": v(-18, 3.71) * mm, "end": v(-10.71, 3.71) * mm});
            skLineSegment(sketch, "E277", {"start": v(-10.71, 3.71) * mm, "end": v(-7, 0) * mm});
            skLineSegment(sketch, "E278", {"start": v(-6.12, -0.87) * mm, "end": v(-4.95, -2.05) * mm});
            skLineSegment(sketch, "E279", {"start": v(-4.95, -2.05) * mm, "end": v(-4.95, -3.71) * mm});
            skLineSegment(sketch, "E280", {"start": v(-4.95, -3.71) * mm, "end": v(-8.96, -3.71) * mm});
            skLineSegment(sketch, "E281", {"start": v(-8.96, -3.71) * mm, "end": v(-6.12, -0.87) * mm});
            skLineSegment(sketch, "E282", {"start": v(-2.05, -4.95) * mm, "end": v(-0.88, -6.12) * mm});
            skLineSegment(sketch, "E283", {"start": v(-0.88, -6.12) * mm, "end": v(-3.71, -8.96) * mm});
            skLineSegment(sketch, "E284", {"start": v(-3.71, -8.96) * mm, "end": v(-3.71, -4.95) * mm});
            skLineSegment(sketch, "E285", {"start": v(-3.71, -4.95) * mm, "end": v(-2.05, -4.95) * mm});
            skLineSegment(sketch, "E286", {"start": v(2.05, -4.95) * mm, "end": v(3.71, -4.95) * mm});
            skLineSegment(sketch, "E287", {"start": v(3.71, -4.95) * mm, "end": v(3.71, -8.96) * mm});
            skLineSegment(sketch, "E288", {"start": v(3.71, -8.96) * mm, "end": v(0.87, -6.12) * mm});
            skLineSegment(sketch, "E289", {"start": v(0.87, -6.12) * mm, "end": v(2.05, -4.95) * mm});
            skLineSegment(sketch, "E290", {"start": v(4.95, -2.05) * mm, "end": v(6.12, -0.87) * mm});
            skLineSegment(sketch, "E291", {"start": v(6.12, -0.87) * mm, "end": v(8.96, -3.71) * mm});
            skLineSegment(sketch, "E292", {"start": v(8.96, -3.71) * mm, "end": v(4.95, -3.71) * mm});
            skLineSegment(sketch, "E293", {"start": v(18, 3.71) * mm, "end": v(14.28, 0) * mm});
            skLineSegment(sketch, "E294", {"start": v(14.28, 0) * mm, "end": v(18, -3.71) * mm});
            skLineSegment(sketch, "E295", {"start": v(18, -3.71) * mm, "end": v(10.7, -3.71) * mm});
            skLineSegment(sketch, "E296", {"start": v(10.7, -3.71) * mm, "end": v(7, 0) * mm});
            skLineSegment(sketch, "E297", {"start": v(19.23, 4.95) * mm, "end": v(11.95, 4.95) * mm});
            skLineSegment(sketch, "E298", {"start": v(11.95, 4.95) * mm, "end": v(17.1, 10.1) * mm});
            skLineSegment(sketch, "E299", {"start": v(17.1, 10.1) * mm, "end": v(24.38, 10.1) * mm});
            skLineSegment(sketch, "E300", {"start": v(24.38, 10.1) * mm, "end": v(19.23, 4.95) * mm});
            skLineSegment(sketch, "E301", {"start": v(16.67, 11.42) * mm, "end": v(16.59, 11.34) * mm});
            skLineSegment(sketch, "E302", {"start": v(16.59, 11.34) * mm, "end": v(11.34, 11.34) * mm});
            skLineSegment(sketch, "E303", {"start": v(11.34, 11.34) * mm, "end": v(11.34, 16.59) * mm});
            skLineSegment(sketch, "E304", {"start": v(11.34, 16.59) * mm, "end": v(11.42, 16.67) * mm});
            skLineSegment(sketch, "E305", {"start": v(11.42, 16.67) * mm, "end": v(16.86, 16.86) * mm});
            skLineSegment(sketch, "E306", {"start": v(16.86, 16.86) * mm, "end": v(16.67, 11.42) * mm});
            skLineSegment(sketch, "E307", {"start": v(15.35, 10.1) * mm, "end": v(10.2, 4.95) * mm});
            skLineSegment(sketch, "E308", {"start": v(10.2, 4.95) * mm, "end": v(4.95, 4.95) * mm});
            skLineSegment(sketch, "E309", {"start": v(4.95, 4.95) * mm, "end": v(4.95, 10.2) * mm});
            skLineSegment(sketch, "E310", {"start": v(4.95, 10.2) * mm, "end": v(10.1, 15.35) * mm});
            skLineSegment(sketch, "E311", {"start": v(10.1, 15.35) * mm, "end": v(10.1, 10.1) * mm});
            skLineSegment(sketch, "E312", {"start": v(10.1, 10.1) * mm, "end": v(15.35, 10.1) * mm});
            skLineSegment(sketch, "E313", {"start": v(-4.95, 11.95) * mm, "end": v(-10.1, 17.1) * mm});
            skLineSegment(sketch, "E314", {"start": v(-10.1, 17.1) * mm, "end": v(-10.1, 24.39) * mm});
            skLineSegment(sketch, "E315", {"start": v(-10.1, 24.39) * mm, "end": v(-4.95, 19.23) * mm});
            skLineSegment(sketch, "E316", {"start": v(-4.95, 19.23) * mm, "end": v(-4.95, 11.95) * mm});
            skLineSegment(sketch, "E317", {"start": v(-4.95, 10.2) * mm, "end": v(-4.95, 4.95) * mm});
            skLineSegment(sketch, "E318", {"start": v(-4.95, 4.95) * mm, "end": v(-10.2, 4.95) * mm});
            skLineSegment(sketch, "E319", {"start": v(-10.2, 4.95) * mm, "end": v(-15.35, 10.1) * mm});
            skLineSegment(sketch, "E320", {"start": v(-15.35, 10.1) * mm, "end": v(-10.1, 10.1) * mm});
            skLineSegment(sketch, "E321", {"start": v(-10.1, 10.1) * mm, "end": v(-10.1, 15.35) * mm});
            skLineSegment(sketch, "E322", {"start": v(-10.1, 15.35) * mm, "end": v(-4.95, 10.2) * mm});
            skLineSegment(sketch, "E323", {"start": v(-17.1, 10.1) * mm, "end": v(-11.95, 4.95) * mm});
            skLineSegment(sketch, "E324", {"start": v(-11.95, 4.95) * mm, "end": v(-19.23, 4.95) * mm});
            skLineSegment(sketch, "E325", {"start": v(-19.23, 4.95) * mm, "end": v(-24.39, 10.1) * mm});
            skLineSegment(sketch, "E326", {"start": v(-24.39, 10.1) * mm, "end": v(-17.1, 10.1) * mm});
            skLineSegment(sketch, "E327", {"start": v(-19.23, -4.95) * mm, "end": v(-11.95, -4.95) * mm});
            skLineSegment(sketch, "E328", {"start": v(-11.95, -4.95) * mm, "end": v(-17.1, -10.1) * mm});
            skLineSegment(sketch, "E329", {"start": v(-17.1, -10.1) * mm, "end": v(-24.39, -10.1) * mm});
            skLineSegment(sketch, "E330", {"start": v(-24.39, -10.1) * mm, "end": v(-19.23, -4.95) * mm});
            skLineSegment(sketch, "E331", {"start": v(-16.67, -11.42) * mm, "end": v(-16.59, -11.34) * mm});
            skLineSegment(sketch, "E332", {"start": v(-16.59, -11.34) * mm, "end": v(-11.34, -11.34) * mm});
            skLineSegment(sketch, "E333", {"start": v(-11.34, -11.34) * mm, "end": v(-11.34, -16.59) * mm});
            skLineSegment(sketch, "E334", {"start": v(-11.34, -16.59) * mm, "end": v(-11.42, -16.67) * mm});
            skLineSegment(sketch, "E335", {"start": v(-11.42, -16.67) * mm, "end": v(-16.86, -16.86) * mm});
            skLineSegment(sketch, "E336", {"start": v(-16.86, -16.86) * mm, "end": v(-16.67, -11.42) * mm});
            skLineSegment(sketch, "E337", {"start": v(-15.35, -10.1) * mm, "end": v(-10.2, -4.95) * mm});
            skLineSegment(sketch, "E338", {"start": v(-10.2, -4.95) * mm, "end": v(-4.95, -4.95) * mm});
            skLineSegment(sketch, "E339", {"start": v(-4.95, -4.95) * mm, "end": v(-4.95, -10.2) * mm});
            skLineSegment(sketch, "E340", {"start": v(-4.95, -10.2) * mm, "end": v(-10.1, -15.35) * mm});
            skLineSegment(sketch, "E341", {"start": v(-10.1, -15.35) * mm, "end": v(-10.1, -10.1) * mm});
            skLineSegment(sketch, "E342", {"start": v(-10.1, -10.1) * mm, "end": v(-15.35, -10.1) * mm});
            skLineSegment(sketch, "E343", {"start": v(4.95, -11.95) * mm, "end": v(10.1, -17.1) * mm});
            skLineSegment(sketch, "E344", {"start": v(10.1, -17.1) * mm, "end": v(10.1, -24.38) * mm});
            skLineSegment(sketch, "E345", {"start": v(10.1, -24.38) * mm, "end": v(4.95, -19.23) * mm});
            skLineSegment(sketch, "E346", {"start": v(4.95, -19.23) * mm, "end": v(4.95, -11.95) * mm});
            skLineSegment(sketch, "E347", {"start": v(4.95, -10.2) * mm, "end": v(4.95, -4.95) * mm});
            skLineSegment(sketch, "E348", {"start": v(4.95, -4.95) * mm, "end": v(10.2, -4.95) * mm});
            skLineSegment(sketch, "E349", {"start": v(10.2, -4.95) * mm, "end": v(15.35, -10.1) * mm});
            skLineSegment(sketch, "E350", {"start": v(15.35, -10.1) * mm, "end": v(10.1, -10.1) * mm});
            skLineSegment(sketch, "E351", {"start": v(10.1, -10.1) * mm, "end": v(10.1, -15.35) * mm});
            skLineSegment(sketch, "E352", {"start": v(10.1, -15.35) * mm, "end": v(4.95, -10.2) * mm});
            skLineSegment(sketch, "E353", {"start": v(17.1, -10.1) * mm, "end": v(11.95, -4.95) * mm});
            skLineSegment(sketch, "E354", {"start": v(11.95, -4.95) * mm, "end": v(19.23, -4.95) * mm});
            skLineSegment(sketch, "E355", {"start": v(19.23, -4.95) * mm, "end": v(24.38, -10.1) * mm});
            skLineSegment(sketch, "E356", {"start": v(24.38, -10.1) * mm, "end": v(17.1, -10.1) * mm});
            skLineSegment(sketch, "E357", {"start": v(25.66, -9.63) * mm, "end": v(20.68, -4.64) * mm});
            skLineSegment(sketch, "E358", {"start": v(20.68, -4.64) * mm, "end": v(25.65, 0) * mm});
            skLineSegment(sketch, "E359", {"start": v(25.65, 0) * mm, "end": v(20.68, 4.64) * mm});
            skLineSegment(sketch, "E360", {"start": v(20.68, 4.64) * mm, "end": v(25.66, 9.63) * mm});
            skLineSegment(sketch, "E361", {"start": v(25.66, 9.63) * mm, "end": v(35.29, 0) * mm});
            skLineSegment(sketch, "E362", {"start": v(35.29, 0) * mm, "end": v(25.66, -9.63) * mm});
            skLineSegment(sketch, "E363", {"start": v(24.95, 11.34) * mm, "end": v(17.9, 11.34) * mm});
            skLineSegment(sketch, "E364", {"start": v(17.9, 11.34) * mm, "end": v(18.14, 18.14) * mm});
            skLineSegment(sketch, "E365", {"start": v(18.14, 18.14) * mm, "end": v(11.34, 17.9) * mm});
            skLineSegment(sketch, "E366", {"start": v(11.34, 17.9) * mm, "end": v(11.34, 24.95) * mm});
            skLineSegment(sketch, "E367", {"start": v(11.34, 24.95) * mm, "end": v(24.95, 24.95) * mm});
            skLineSegment(sketch, "E368", {"start": v(24.95, 24.95) * mm, "end": v(24.95, 11.34) * mm});
            skLineSegment(sketch, "E369", {"start": v(0, 35.29) * mm, "end": v(9.63, 25.66) * mm});
            skLineSegment(sketch, "E370", {"start": v(9.63, 25.66) * mm, "end": v(4.64, 20.68) * mm});
            skLineSegment(sketch, "E371", {"start": v(4.64, 20.68) * mm, "end": v(0, 25.65) * mm});
            skLineSegment(sketch, "E372", {"start": v(0, 25.65) * mm, "end": v(-4.64, 20.68) * mm});
            skLineSegment(sketch, "E373", {"start": v(-4.64, 20.68) * mm, "end": v(-9.63, 25.66) * mm});
            skLineSegment(sketch, "E374", {"start": v(-9.63, 25.66) * mm, "end": v(0, 35.29) * mm});
            skLineSegment(sketch, "E375", {"start": v(-24.95, 24.95) * mm, "end": v(-11.34, 24.95) * mm});
            skLineSegment(sketch, "E376", {"start": v(-11.34, 24.95) * mm, "end": v(-11.34, 17.9) * mm});
            skLineSegment(sketch, "E377", {"start": v(-11.34, 17.9) * mm, "end": v(-18.14, 18.14) * mm});
            skLineSegment(sketch, "E378", {"start": v(-18.14, 18.14) * mm, "end": v(-17.9, 11.34) * mm});
            skLineSegment(sketch, "E379", {"start": v(-17.9, 11.34) * mm, "end": v(-24.95, 11.34) * mm});
            skLineSegment(sketch, "E380", {"start": v(-24.95, 11.34) * mm, "end": v(-24.95, 24.95) * mm});
            skLineSegment(sketch, "E381", {"start": v(-25.66, 9.63) * mm, "end": v(-20.68, 4.64) * mm});
            skLineSegment(sketch, "E382", {"start": v(-20.68, 4.64) * mm, "end": v(-25.65, 0) * mm});
            skLineSegment(sketch, "E383", {"start": v(-25.65, 0) * mm, "end": v(-20.68, -4.64) * mm});
            skLineSegment(sketch, "E384", {"start": v(-20.68, -4.64) * mm, "end": v(-25.66, -9.63) * mm});
            skLineSegment(sketch, "E385", {"start": v(-25.66, -9.63) * mm, "end": v(-35.29, 0) * mm});
            skLineSegment(sketch, "E386", {"start": v(-35.29, 0) * mm, "end": v(-25.66, 9.63) * mm});
            skLineSegment(sketch, "E387", {"start": v(0, -35.29) * mm, "end": v(-9.63, -25.66) * mm});
            skLineSegment(sketch, "E388", {"start": v(-9.63, -25.66) * mm, "end": v(-4.64, -20.68) * mm});
            skLineSegment(sketch, "E389", {"start": v(-4.64, -20.68) * mm, "end": v(0, -25.65) * mm});
            skLineSegment(sketch, "E390", {"start": v(0, -25.65) * mm, "end": v(4.64, -20.68) * mm});
            skLineSegment(sketch, "E391", {"start": v(4.64, -20.68) * mm, "end": v(9.63, -25.66) * mm});
            skLineSegment(sketch, "E392", {"start": v(9.63, -25.66) * mm, "end": v(0, -35.29) * mm});
            skLineSegment(sketch, "E393", {"start": v(24.95, -24.95) * mm, "end": v(11.34, -24.95) * mm});
            skLineSegment(sketch, "E394", {"start": v(11.34, -24.95) * mm, "end": v(11.34, -17.9) * mm});
            skLineSegment(sketch, "E395", {"start": v(11.34, -17.9) * mm, "end": v(18.14, -18.14) * mm});
            skLineSegment(sketch, "E396", {"start": v(18.14, -18.14) * mm, "end": v(17.9, -11.34) * mm});
            skLineSegment(sketch, "E397", {"start": v(17.9, -11.34) * mm, "end": v(24.95, -11.34) * mm});
            skLineSegment(sketch, "E398", {"start": v(24.95, -11.34) * mm, "end": v(24.95, -24.95) * mm});
            skLineSegment(sketch, "E399.MirrorCS", {"start": v(-11.34, -24.95) * mm, "end": v(-24.95, -24.95) * mm});
            skLineSegment(sketch, "E400.MirrorCS", {"start": v(-11.34, -17.9) * mm, "end": v(-11.34, -24.95) * mm});
            skLineSegment(sketch, "E401.MirrorCS", {"start": v(-11.34, -17.9) * mm, "end": v(-18.14, -18.14) * mm});
            skLineSegment(sketch, "E402.MirrorCS", {"start": v(-18.14, -18.14) * mm, "end": v(-17.9, -11.34) * mm});
            skLineSegment(sketch, "E403.MirrorCS", {"start": v(-24.95, -24.95) * mm, "end": v(-24.95, -11.34) * mm});
            skLineSegment(sketch, "E404.MirrorCS", {"start": v(-17.9, -11.34) * mm, "end": v(-24.95, -11.34) * mm});
            skLineSegment(sketch, "E405.MirrorCS", {"start": v(-16.85, 16.86) * mm, "end": v(-11.42, 16.67) * mm});
            skLineSegment(sketch, "E406.MirrorCS", {"start": v(-11.34, 16.59) * mm, "end": v(-11.34, 11.34) * mm});
            skLineSegment(sketch, "E407.MirrorCS", {"start": v(-11.34, 11.34) * mm, "end": v(-16.59, 11.34) * mm});
            skLineSegment(sketch, "E408.MirrorCS", {"start": v(-16.67, 11.42) * mm, "end": v(-16.85, 16.86) * mm});
            skLineSegment(sketch, "E409", {"start": v(-11.42, 16.67) * mm, "end": v(-11.34, 16.59) * mm});
            skLineSegment(sketch, "E410", {"start": v(-16.67, 11.42) * mm, "end": v(-16.59, 11.34) * mm});
            skCircle(sketch, "E411", {"center": v(0, 0) * mm, "radius": 44.45 * mm});
            skSolve(sketch);
        }
        {
            var Q0;
            Q0 = qSketchRegion(id + "F2", true);
            extrude(context, id + "F3", {"entities" : qUnion([Q0]), "operationType" : NewBodyOperationType.INTERSECT, "endBound" : BoundingType.UP_TO_NEXT, "oppositeDirection" : true, "depth" : 25.4 * mm});
        }
    });
